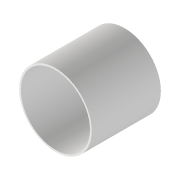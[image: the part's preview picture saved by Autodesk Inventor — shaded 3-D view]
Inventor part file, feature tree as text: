
AUTODESK INVENTOR PART (.ipt)
format: ipt  version: 2020 (Build 240168000, 168)  size: 88,576 bytes
history: native  units: mm
features: extrude x1, sketch x1
ambient origin geometry x8: Origin, YZ Plane, XZ Plane, XY Plane, X Axis, Y Axis, Z Axis, Center Point
bodies: Volumenkörper1 (feature_tree)
feature tree (2):
  extrude  "Extrusion1"  Depth=200.0mm
  sketch  "Skizze1"  dims[d0=200.0mm d1=210.0mm d2=200.0mm d3=0.0mm]
